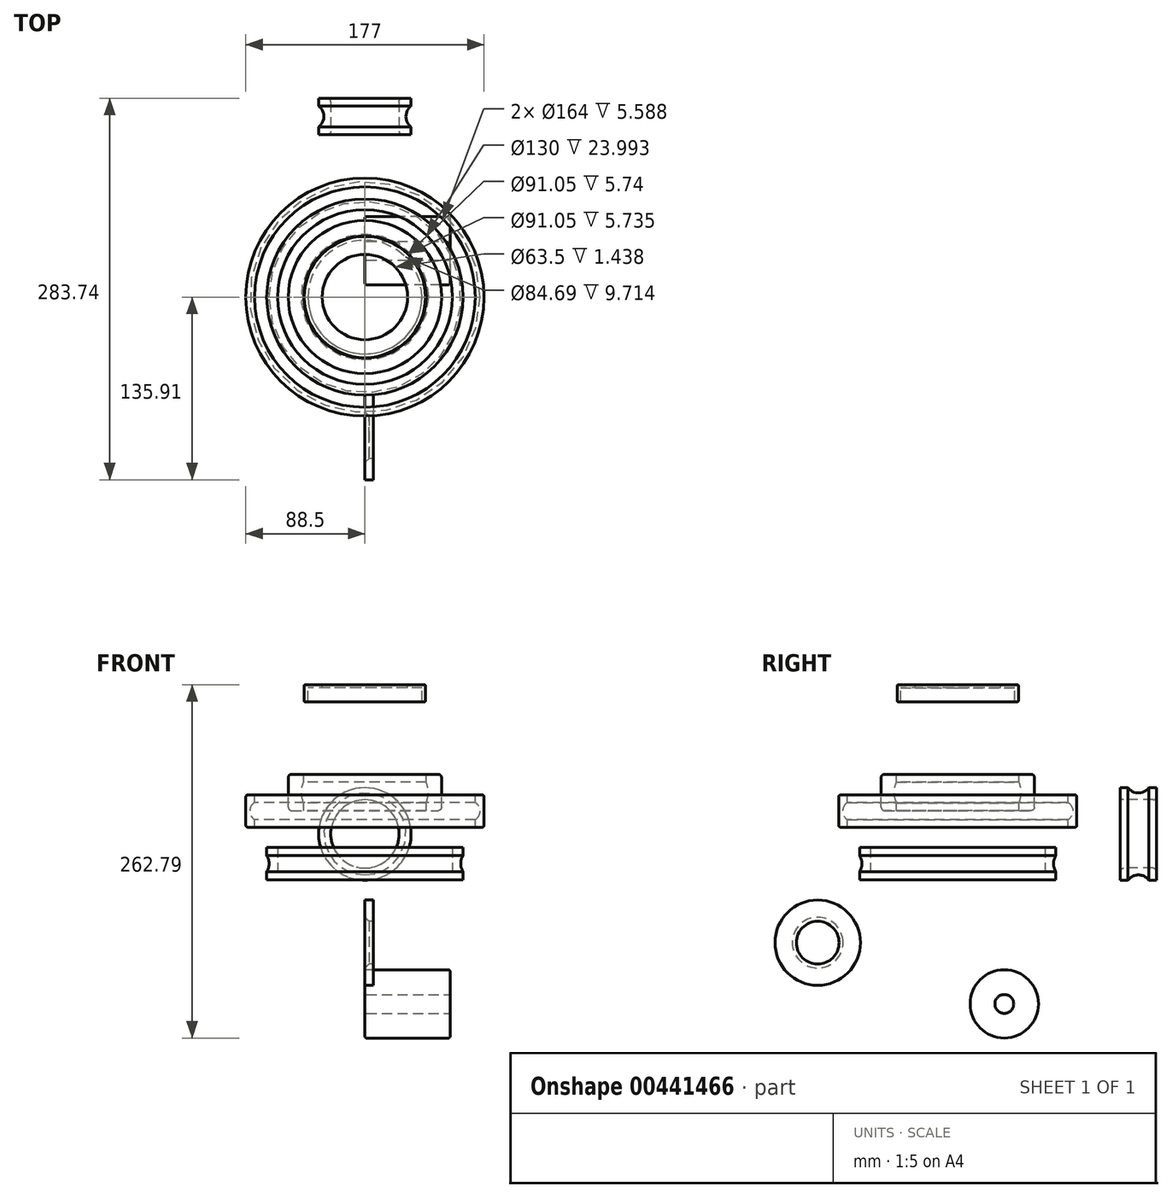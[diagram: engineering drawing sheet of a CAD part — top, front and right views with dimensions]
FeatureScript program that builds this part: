
annotation { "Feature Type Name" : "Feature", "Feature Type Description" : "" }
export const myFeature = defineFeature(function(context is Context, id is Id, definition is map)
    precondition{}
    {
        {
            var Q0;
            Q0=qCreatedBy(makeId("Front.planeOp"),FACE);
            var sketch = newSketch(context, id + "F0", { "sketchPlane" : qUnion([Q0])});
            skLineSegment(sketch, "E0", {"start": v(0, 61.58) * mm, "end": v(0, -62.26) * mm, "construction": true});
            skLineSegment(sketch, "E1", {"start": v(82, 29) * mm, "end": v(88.5, 29) * mm});
            skLineSegment(sketch, "E2", {"start": v(88.5, 29) * mm, "end": v(88.5, 5.02) * mm});
            skLineSegment(sketch, "E3", {"start": v(88.5, 5.02) * mm, "end": v(82, 5.02) * mm});
            skLineSegment(sketch, "E4", {"start": v(82, 5.02) * mm, "end": v(82, 10.6) * mm});
            skLineSegment(sketch, "E5", {"start": v(82, 29) * mm, "end": v(82, 23.4) * mm});
            skArc(sketch, "E6", {"start": v(82, 10.6) * mm, "mid": v(85.6, 17) * mm, "end": v(82, 23.4) * mm});
            skSolve(sketch);
        }
        {
            var Q0;
            Q0=makeQuery(id+"F0.imprint","IMPRINT",FACE,{"disambiguationData":[TD([[makeQuery(id+"F0.imprint","IMPRINT",EDGE,{"derivedFrom":sQuery(id+"F0.wireOp",EDGE,"E1")}),-1.0]])]});
            var Q1;
            Q1=sQuery(id+"F0.wireOp",EDGE,"E0");
            revolve(context, id + "F1", {"entities" : qUnion([Q0]), "axis" : qUnion([Q1]), "revolveType" : RevolveType.FULL});
        }
        {
            var Q0;
            Q0=makeQuery(id+"F1.opRevolve","SWEPT_EDGE",EDGE,{"disambiguationData":[OSD([sQuery(id+"F0.wireOp",EDGE,"E2"),sQuery(id+"F0.wireOp",EDGE,"E3")])]});
            var Q1;
            Q1=makeQuery(id+"F1.opRevolve","SWEPT_EDGE",EDGE,{"disambiguationData":[OSD([sQuery(id+"F0.wireOp",EDGE,"E1"),sQuery(id+"F0.wireOp",EDGE,"E2")])]});
            fillet(context, id + "F2", {"entities" : qUnion([Q0, Q1]), "radius" : 1.27 * mm, "tangentPropagation" : true, "allowEdgeOverflow" : false});
        }
        {
            var Q0;
            Q0=qCreatedBy(makeId("Front.planeOp"),FACE);
            var sketch = newSketch(context, id + "F3", { "sketchPlane" : qUnion([Q0])});
            skLineSegment(sketch, "E7", {"start": v(0, -71.48) * mm, "end": v(0, 72.14) * mm, "construction": true});
            skLineSegment(sketch, "E8", {"start": v(-65, -34.09) * mm, "end": v(-65, -10.1) * mm});
            skLineSegment(sketch, "E9", {"start": v(-65, -34.09) * mm, "end": v(-72.94, -34.09) * mm});
            skLineSegment(sketch, "E10", {"start": v(-72.94, -34.09) * mm, "end": v(-72.94, -27.98) * mm});
            skLineSegment(sketch, "E11", {"start": v(-65, -10.1) * mm, "end": v(-72.94, -10.1) * mm});
            skLineSegment(sketch, "E12", {"start": v(-72.94, -10.1) * mm, "end": v(-72.94, -16.2) * mm});
            skArc(sketch, "E13", {"start": v(-72.94, -27.98) * mm, "mid": v(-71.23, -22.09) * mm, "end": v(-72.94, -16.2) * mm});
            skSolve(sketch);
        }
        {
            var Q0;
            Q0=makeQuery(id+"F3.imprint","IMPRINT",FACE,{"disambiguationData":[TD([[makeQuery(id+"F3.imprint","IMPRINT",EDGE,{"derivedFrom":sQuery(id+"F3.wireOp",EDGE,"E8")}),1.0]])]});
            var Q1;
            Q1=sQuery(id+"F3.wireOp",EDGE,"E7");
            revolve(context, id + "F4", {"entities" : qUnion([Q0]), "axis" : qUnion([Q1]), "revolveType" : RevolveType.FULL});
        }
        {
            var Q0;
            Q0=qCreatedBy(makeId("Right.planeOp"),FACE);
            var sketch = newSketch(context, id + "F5", { "sketchPlane" : qUnion([Q0])});
            skCircle(sketch, "E14", {"center": v(34.6, -126.43) * mm, "radius": 25.4 * mm});
            skSolve(sketch);
        }
        {
            var Q0;
            Q0=makeQuery(id+"F5.imprint","IMPRINT",FACE,{"disambiguationData":[TD([[makeQuery(id+"F5.imprint","IMPRINT",EDGE,{"derivedFrom":sQuery(id+"F5.wireOp",EDGE,"E14")}),1.0]])]});
            extrude(context, id + "F6", {"entities" : qUnion([Q0]), "depth" : 63.35 * mm});
        }
        {
            var Q0;
            Q0=makeQuery(id+"F6.opExtrude","CAP_FACE",FACE,{"disambiguationData":[OSD([sQuery(id+"F5.wireOp",EDGE,"E14")])],"isStart":false});
            var sketch = newSketch(context, id + "F7", { "sketchPlane" : qUnion([Q0])});
            skCircle(sketch, "E15", {"center": v(34.6, -126.43) * mm, "radius": 7 * mm});
            skSolve(sketch);
        }
        {
            var Q0;
            Q0=makeQuery(id+"F7.imprint","IMPRINT",FACE,{"disambiguationData":[TD([[makeQuery(id+"F7.imprint","IMPRINT",EDGE,{"derivedFrom":sQuery(id+"F7.wireOp",EDGE,"E15")}),1.0]])]});
            extrude(context, id + "F8", {"entities" : qUnion([Q0]), "operationType" : NewBodyOperationType.REMOVE, "oppositeDirection" : true, "depth" : 159.26 * mm});
        }
        {
            var Q0;
            Q0=makeQuery(id+"F6.opExtrude","CAP_EDGE",EDGE,{"disambiguationData":[OSD([sQuery(id+"F5.wireOp",EDGE,"E14")])],"isStart":false});
            var Q1;
            Q1=makeQuery(id+"F8.boolean.opBoolean","COPY",EDGE,{"derivedFrom":makeQuery(id+"F8.opExtrude","CAP_EDGE",EDGE,{"disambiguationData":[OSD([sQuery(id+"F7.wireOp",EDGE,"E15")])],"isStart":true})});
            var Q2;
            Q2=makeQuery(id+"F6.opExtrude","CAP_EDGE",EDGE,{"disambiguationData":[OSD([sQuery(id+"F5.wireOp",EDGE,"E14")])],"isStart":true});
            var Q3;
            Q3=makeQuery(id+"F8.boolean.opBoolean","INTERSECT",EDGE,{"derivedFrom":[makeQuery(id+"F6.opExtrude","CAP_FACE",FACE,{"disambiguationData":[OSD([sQuery(id+"F5.wireOp",EDGE,"E14")])],"isStart":true}),makeQuery(id+"F8.opExtrude","SWEPT_FACE",FACE,{"disambiguationData":[OSD([sQuery(id+"F7.wireOp",EDGE,"E15")])]})]});
            fillet(context, id + "F9", {"entities" : qUnion([Q0, Q1, Q2, Q3]), "radius" : 1.27 * mm, "tangentPropagation" : true, "allowEdgeOverflow" : false});
        }
        {
            var Q0;
            Q0=qCreatedBy(makeId("Right.planeOp"),FACE);
            var sketch = newSketch(context, id + "F10", { "sketchPlane" : qUnion([Q0])});
            skLineSegment(sketch, "E16", {"start": v(-56.95, 44.41) * mm, "end": v(-56.95, 17.36) * mm});
            skLineSegment(sketch, "E17", {"start": v(-56.95, 44.41) * mm, "end": v(-45.52, 44.41) * mm});
            skLineSegment(sketch, "E18", {"start": v(-45.52, 44.41) * mm, "end": v(-45.52, 38.68) * mm});
            skLineSegment(sketch, "E19", {"start": v(-56.95, 17.36) * mm, "end": v(-45.52, 17.36) * mm});
            skLineSegment(sketch, "E20", {"start": v(0, 76.08) * mm, "end": v(0, -77.08) * mm, "construction": true});
            skLineSegment(sketch, "E21", {"start": v(-45.52, 17.36) * mm, "end": v(-45.52, 23.1) * mm});
            skArc(sketch, "E22", {"start": v(-45.52, 38.68) * mm, "mid": v(-47.12, 30.9) * mm, "end": v(-45.52, 23.1) * mm});
            skSolve(sketch);
        }
        {
            var Q0;
            Q0=makeQuery(id+"F10.imprint","IMPRINT",FACE,{"disambiguationData":[TD([[makeQuery(id+"F10.imprint","IMPRINT",EDGE,{"derivedFrom":sQuery(id+"F10.wireOp",EDGE,"E16")}),1.0]])]});
            var Q1;
            Q1=sQuery(id+"F10.wireOp",EDGE,"E20");
            revolve(context, id + "F11", {"entities" : qUnion([Q0]), "axis" : qUnion([Q1]), "revolveType" : RevolveType.FULL});
        }
        {
            var Q0;
            Q0=makeQuery(id+"F11.opRevolve","SWEPT_EDGE",EDGE,{"disambiguationData":[OSD([sQuery(id+"F10.wireOp",EDGE,"E16"),sQuery(id+"F10.wireOp",EDGE,"E17")])]});
            var Q1;
            Q1=makeQuery(id+"F11.opRevolve","SWEPT_EDGE",EDGE,{"disambiguationData":[OSD([sQuery(id+"F10.wireOp",EDGE,"E16"),sQuery(id+"F10.wireOp",EDGE,"E19")])]});
            fillet(context, id + "F12", {"entities" : qUnion([Q0, Q1]), "radius" : 2.54 * mm, "tangentPropagation" : true, "allowEdgeOverflow" : false});
        }
        {
            var Q0;
            Q0=qCreatedBy(makeId("Front.planeOp"),FACE);
            var sketch = newSketch(context, id + "F13", { "sketchPlane" : qUnion([Q0])});
            skLineSegment(sketch, "E23", {"start": v(-31.75, 110.96) * mm, "end": v(-45.07, 110.96) * mm});
            skLineSegment(sketch, "E24", {"start": v(-45.07, 110.96) * mm, "end": v(-45.07, 98.26) * mm});
            skLineSegment(sketch, "E25", {"start": v(-31.75, 110.96) * mm, "end": v(-31.75, 108.77) * mm});
            skLineSegment(sketch, "E26", {"start": v(-31.75, 108.77) * mm, "end": v(-42.35, 108.77) * mm});
            skLineSegment(sketch, "E27", {"start": v(-42.35, 108.77) * mm, "end": v(-42.35, 98.3) * mm});
            skLineSegment(sketch, "E28", {"start": v(0, 118.02) * mm, "end": v(0, -117.13) * mm, "construction": true});
            skLineSegment(sketch, "E29", {"start": v(-42.35, 98.3) * mm, "end": v(-45.07, 98.26) * mm});
            skSolve(sketch);
        }
        {
            var Q0;
            Q0=makeQuery(id+"F13.imprint","IMPRINT",FACE,{"disambiguationData":[TD([[makeQuery(id+"F13.imprint","IMPRINT",EDGE,{"derivedFrom":sQuery(id+"F13.wireOp",EDGE,"E23")}),1.0]])]});
            var Q1;
            Q1=sQuery(id+"F13.wireOp",EDGE,"E28");
            revolve(context, id + "F14", {"entities" : qUnion([Q0]), "axis" : qUnion([Q1]), "revolveType" : RevolveType.FULL});
        }
        {
            var Q0;
            Q0=makeQuery(id+"F14.opRevolve","SWEPT_EDGE",EDGE,{"disambiguationData":[OSD([sQuery(id+"F13.wireOp",EDGE,"E23"),sQuery(id+"F13.wireOp",EDGE,"E25")])]});
            var Q1;
            Q1=makeQuery(id+"F14.opRevolve","SWEPT_EDGE",EDGE,{"disambiguationData":[OSD([sQuery(id+"F13.wireOp",EDGE,"E24"),sQuery(id+"F13.wireOp",EDGE,"E29")])]});
            var Q2;
            Q2=makeQuery(id+"F14.opRevolve","SWEPT_EDGE",EDGE,{"disambiguationData":[OSD([sQuery(id+"F13.wireOp",EDGE,"E23"),sQuery(id+"F13.wireOp",EDGE,"E24")])]});
            var Q3;
            Q3=makeQuery(id+"F14.opRevolve","SWEPT_EDGE",EDGE,{"disambiguationData":[OSD([sQuery(id+"F13.wireOp",EDGE,"E27"),sQuery(id+"F13.wireOp",EDGE,"E29")])]});
            fillet(context, id + "F15", {"entities" : qUnion([Q0, Q1, Q2, Q3]), "radius" : 0.76 * mm, "tangentPropagation" : true, "allowEdgeOverflow" : false});
        }
        {
            var Q0;
            Q0=qCreatedBy(makeId("Right.planeOp"),FACE);
            var sketch = newSketch(context, id + "F16", { "sketchPlane" : qUnion([Q0])});
            skCircle(sketch, "E30", {"center": v(-104.16, -80.92) * mm, "radius": 31.75 * mm});
            skSolve(sketch);
        }
        {
            var Q0;
            Q0=makeQuery(id+"F16.imprint","IMPRINT",FACE,{"disambiguationData":[TD([[makeQuery(id+"F16.imprint","IMPRINT",EDGE,{"derivedFrom":sQuery(id+"F16.wireOp",EDGE,"E30")}),1.0]])]});
            extrude(context, id + "F17", {"entities" : qUnion([Q0]), "depth" : 6.35 * mm});
        }
        {
            var Q0;
            Q0=makeQuery(id+"F17.opExtrude","CAP_FACE",FACE,{"disambiguationData":[OSD([sQuery(id+"F16.wireOp",EDGE,"E30")])],"isStart":true});
            var sketch = newSketch(context, id + "F18", { "sketchPlane" : qUnion([Q0])});
            skPoint(sketch, "E31", {"position": v(104.16, -80.92) * mm});
            skSolve(sketch);
        }
        {
            var Q0;
            Q0=sQuery(id+"F18.wireOp",VERTEX,"E31");
            var Q1;
            Q1=makeQuery(id+"F17.opExtrude","SWEPT_BODY",BODY,{"disambiguationData":[OSD([sQuery(id+"F16.wireOp",EDGE,"E30")])]});
            hole(context, id + "F19", {"style" : HoleStyle.C_SINK, "endStyle" : HoleEndStyle.BLIND, "holeDiameter" : 31.75 * mm, "cSinkDiameter" : 37.75 * mm, "cSinkAngle" : 90 * degree, "holeDepth" : 50.8 * mm, "isTappedThrough" : true, "tappedDepth" : 12.7 * mm, "tapClearance" : 3, "startFromSketch" : true, "locations" : qUnion([Q0]), "scope" : qUnion([Q1])});
        }
        {
            var Q0;
            Q0=qCreatedBy(makeId("Right.planeOp"),FACE);
            var sketch = newSketch(context, id + "F20", { "sketchPlane" : qUnion([Q0])});
            skLineSegment(sketch, "E32", {"start": v(0, 0) * mm, "end": v(137.86, 0) * mm, "construction": true});
            skLineSegment(sketch, "E33", {"start": v(147.83, 25.4) * mm, "end": v(120.84, 25.4) * mm});
            skLineSegment(sketch, "E34", {"start": v(147.83, 25.4) * mm, "end": v(147.83, 34.38) * mm});
            skLineSegment(sketch, "E35", {"start": v(147.83, 34.38) * mm, "end": v(142.03, 34.38) * mm});
            skLineSegment(sketch, "E36", {"start": v(120.84, 25.4) * mm, "end": v(120.84, 34.38) * mm});
            skLineSegment(sketch, "E37", {"start": v(120.84, 34.38) * mm, "end": v(126.65, 34.38) * mm});
            skArc(sketch, "E38", {"start": v(126.65, 34.38) * mm, "mid": v(134.34, 30.47) * mm, "end": v(142.03, 34.38) * mm});
            skSolve(sketch);
        }
        {
            var Q0;
            Q0=makeQuery(id+"F20.imprint","IMPRINT",FACE,{"disambiguationData":[TD([[makeQuery(id+"F20.imprint","IMPRINT",EDGE,{"derivedFrom":sQuery(id+"F20.wireOp",EDGE,"E33")}),-1.0]])]});
            var Q1;
            Q1=sQuery(id+"F20.wireOp",EDGE,"E32");
            revolve(context, id + "F21", {"operationType" : NewBodyOperationType.ADD, "entities" : qUnion([Q0]), "axis" : qUnion([Q1]), "revolveType" : RevolveType.FULL});
        }
        {
            var Q0;
            Q0=makeQuery(id+"F21.opRevolve","SWEPT_EDGE",EDGE,{"disambiguationData":[OSD([sQuery(id+"F20.wireOp",EDGE,"E33"),sQuery(id+"F20.wireOp",EDGE,"E34")])]});
            var Q1;
            Q1=makeQuery(id+"F21.opRevolve","SWEPT_EDGE",EDGE,{"disambiguationData":[OSD([sQuery(id+"F20.wireOp",EDGE,"E33"),sQuery(id+"F20.wireOp",EDGE,"E36")])]});
            fillet(context, id + "F22", {"entities" : qUnion([Q0, Q1]), "radius" : 2.54 * mm, "tangentPropagation" : true, "allowEdgeOverflow" : false});
        }
    });
